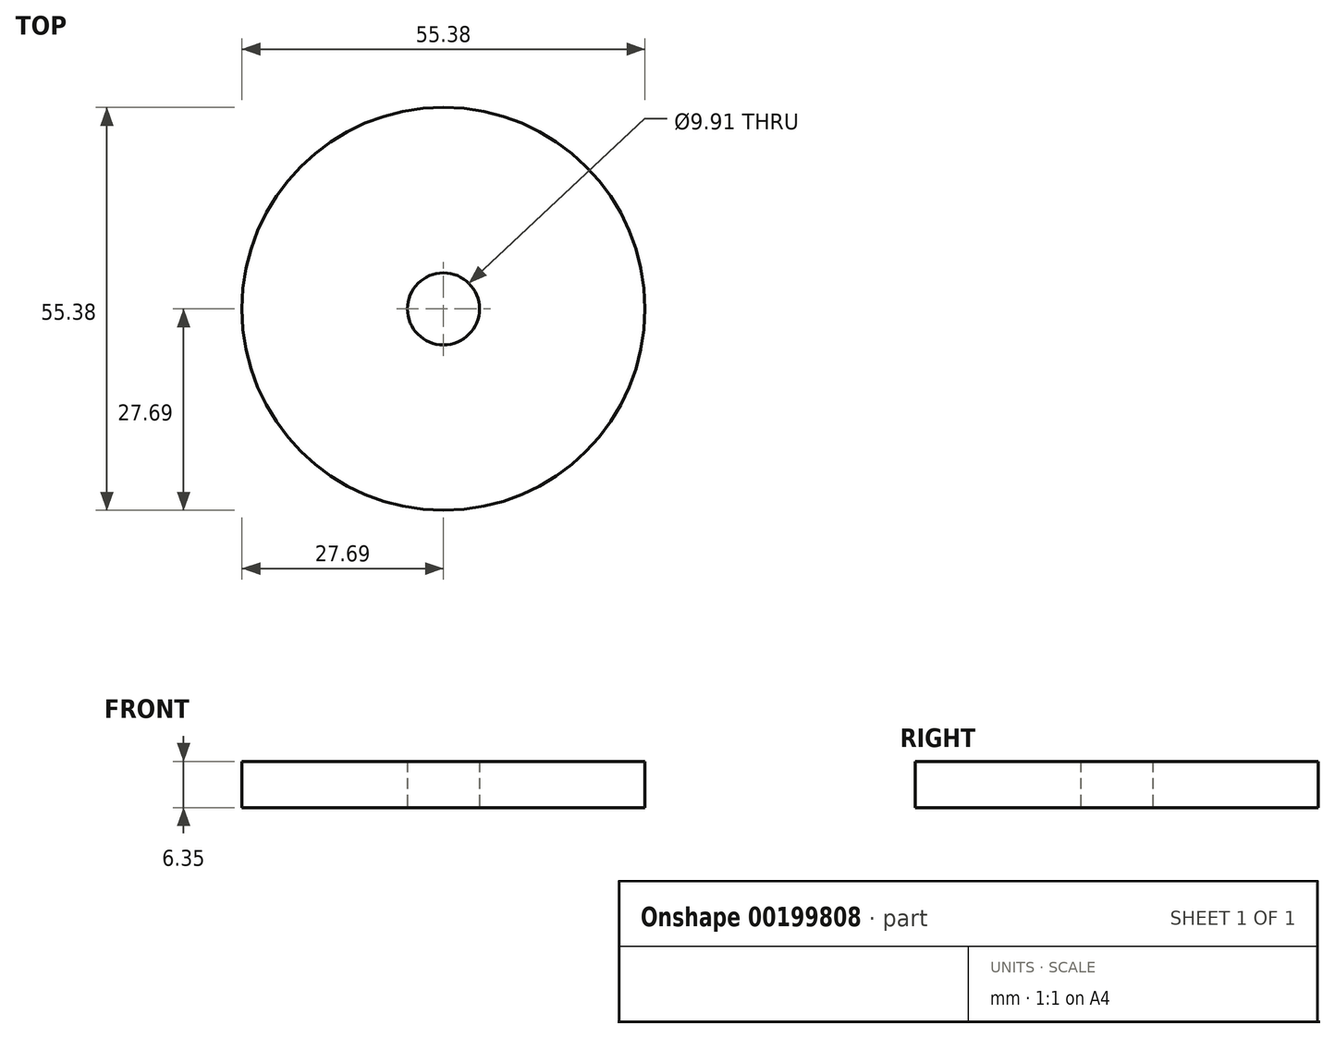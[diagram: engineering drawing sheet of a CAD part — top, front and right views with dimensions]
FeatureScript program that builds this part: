
annotation { "Feature Type Name" : "Feature", "Feature Type Description" : "" }
export const myFeature = defineFeature(function(context is Context, id is Id, definition is map)
    precondition{}
    {
        {
            var Q0;
            Q0=qCreatedBy(makeId("Top.planeOp"),FACE);
            var sketch = newSketch(context, id + "F0", { "sketchPlane" : qUnion([Q0])});
            skCircle(sketch, "E0", {"center": v(0, 0) * mm, "radius": 27.69 * mm});
            skCircle(sketch, "E1", {"center": v(0, 0) * mm, "radius": 4.95 * mm});
            skSolve(sketch);
        }
        {
            var Q0;
            Q0 = qSketchRegion(id + "F0", true);
            extrude(context, id + "F1", {"entities" : qUnion([Q0]), "depth" : 6.35 * mm});
        }
    });
